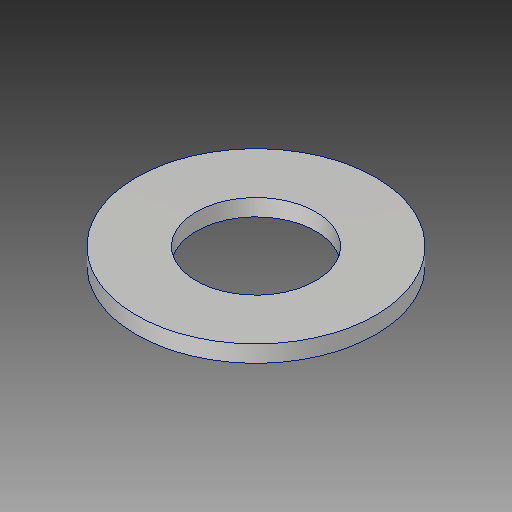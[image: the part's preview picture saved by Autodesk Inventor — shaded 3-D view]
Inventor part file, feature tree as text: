
AUTODESK INVENTOR PART (.ipt)
format: ipt  version: 2017 (Build 210142000, 142)  size: 97,792 bytes
history: native  units: in
note: dims shown in document units (in); Inventor stores cm internally (conversion verified against a paired STEP export)
features: extrude x1, sketch x1
ambient origin geometry x8: Origin, YZ Plane, XZ Plane, XY Plane, X Axis, Y Axis, Z Axis, Center Point
bodies: Solid1 (feature_tree)
feature tree (2):
  extrude  "Extrusion1"  Depth=0.035in
  sketch  "Sketch1"  dims[d0=0.25in d1=0.5in d2=0.035in d3=0.0in]
